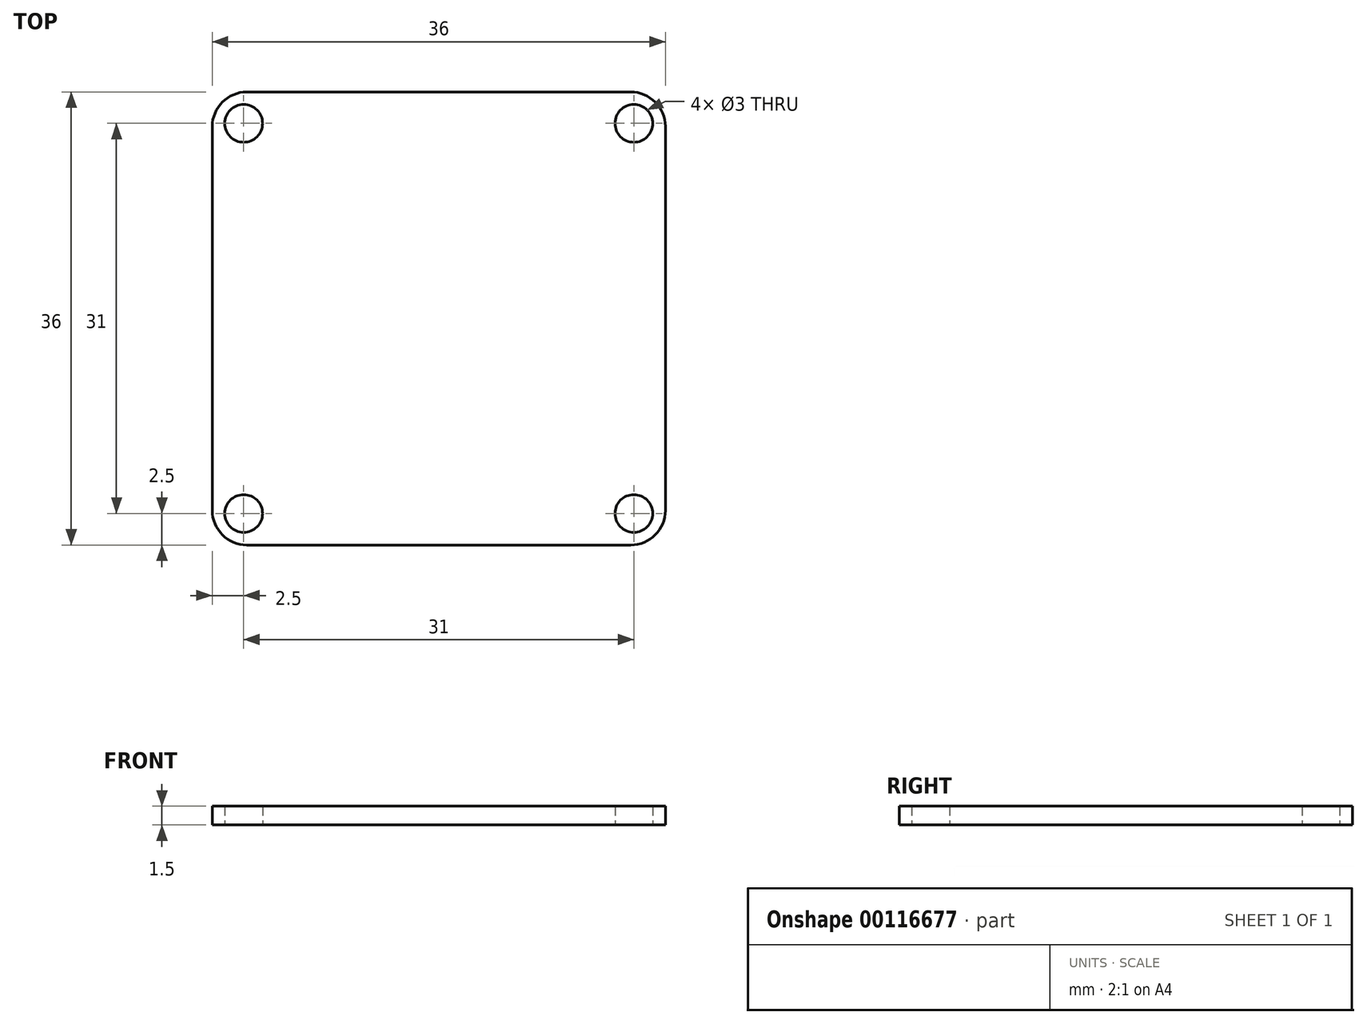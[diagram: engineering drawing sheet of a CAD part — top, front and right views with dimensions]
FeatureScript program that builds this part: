
annotation { "Feature Type Name" : "Feature", "Feature Type Description" : "" }
export const myFeature = defineFeature(function(context is Context, id is Id, definition is map)
    precondition{}
    {
        {
            var Q0;
            Q0=qCreatedBy(makeId("Top.planeOp"),FACE);
            var sketch = newSketch(context, id + "F0", { "sketchPlane" : qUnion([Q0])});
            skLineSegment(sketch, "E0.bottom", {"start": v(2.75, 0) * mm, "end": v(33.25, 0) * mm});
            skLineSegment(sketch, "E0.top", {"start": v(2.75, 36) * mm, "end": v(33.25, 36) * mm});
            skLineSegment(sketch, "E0.left", {"start": v(0, 2.75) * mm, "end": v(0, 33.25) * mm});
            skLineSegment(sketch, "E0.right", {"start": v(36, 2.75) * mm, "end": v(36, 33.25) * mm});
            skLineSegment(sketch, "E1.0", {"start": v(2.5, 2.5) * mm, "end": v(2.5, 33.5) * mm, "construction": true});
            skLineSegment(sketch, "E1.1", {"start": v(2.5, 2.5) * mm, "end": v(33.5, 2.5) * mm, "construction": true});
            skLineSegment(sketch, "E1.2", {"start": v(33.5, 2.5) * mm, "end": v(33.5, 33.5) * mm, "construction": true});
            skLineSegment(sketch, "E1.3", {"start": v(2.5, 33.5) * mm, "end": v(33.5, 33.5) * mm, "construction": true});
            skCircle(sketch, "E2", {"center": v(2.5, 33.5) * mm, "radius": 1.5 * mm});
            skCircle(sketch, "E3", {"center": v(33.5, 33.5) * mm, "radius": 1.5 * mm});
            skCircle(sketch, "E4", {"center": v(2.5, 2.5) * mm, "radius": 1.5 * mm});
            skCircle(sketch, "E5", {"center": v(33.5, 2.5) * mm, "radius": 1.5 * mm});
            skPoint(sketch, "E6.visualSharp", {"position": v(0, 36) * mm});
            skArc(sketch, "E6.filletArc", {"start": v(2.75, 36) * mm, "mid": v(0.8, 35.2) * mm, "end": v(0, 33.25) * mm});
            skPoint(sketch, "E7.visualSharp", {"position": v(36, 36) * mm});
            skArc(sketch, "E7.filletArc", {"start": v(36, 33.25) * mm, "mid": v(35.2, 35.2) * mm, "end": v(33.25, 36) * mm});
            skPoint(sketch, "E8.visualSharp", {"position": v(36, 0) * mm});
            skArc(sketch, "E8.filletArc", {"start": v(33.25, 0) * mm, "mid": v(35.2, 0.8) * mm, "end": v(36, 2.75) * mm});
            skPoint(sketch, "E9.visualSharp", {"position": v(0, 0) * mm});
            skArc(sketch, "E9.filletArc", {"start": v(0, 2.75) * mm, "mid": v(0.8, 0.8) * mm, "end": v(2.75, 0) * mm});
            skSolve(sketch);
        }
        {
            var Q0;
            Q0 = qSketchRegion(id + "F0", true);
            extrude(context, id + "F1", {"entities" : qUnion([Q0]), "depth" : 1.5 * mm});
        }
    });
